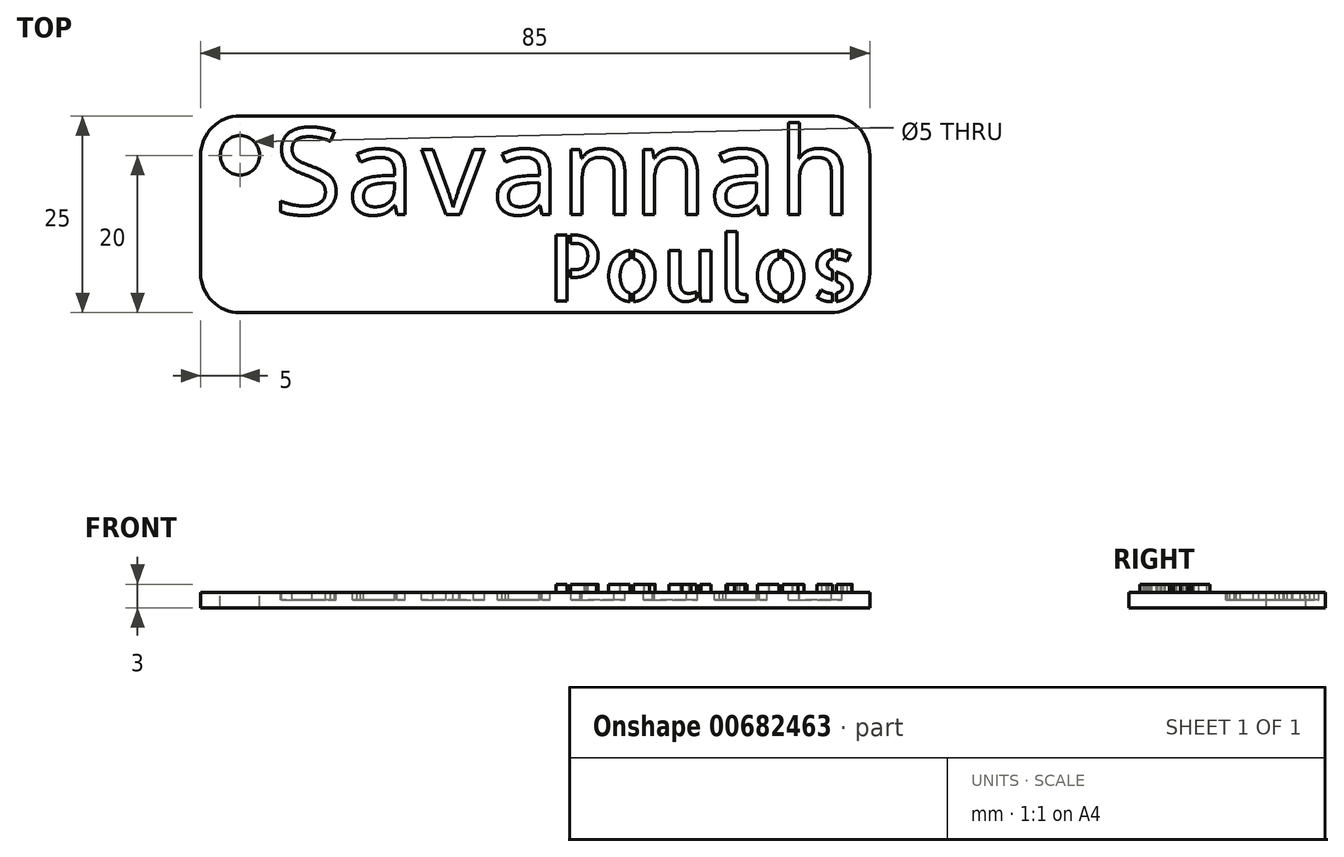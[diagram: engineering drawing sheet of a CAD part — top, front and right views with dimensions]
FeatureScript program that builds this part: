
annotation { "Feature Type Name" : "Feature", "Feature Type Description" : "" }
export const myFeature = defineFeature(function(context is Context, id is Id, definition is map)
    precondition{}
    {
        {
            var Q0;
            Q0=qCreatedBy(makeId("Top.planeOp"),FACE);
            var sketch = newSketch(context, id + "F0", { "sketchPlane" : qUnion([Q0])});
            skLineSegment(sketch, "E0.bottom", {"start": v(37.5, 12.5) * mm, "end": v(-37.5, 12.5) * mm});
            skLineSegment(sketch, "E0.top", {"start": v(37.5, -12.5) * mm, "end": v(-37.5, -12.5) * mm});
            skLineSegment(sketch, "E0.left", {"start": v(42.5, 7.5) * mm, "end": v(42.5, -7.5) * mm});
            skLineSegment(sketch, "E0.right", {"start": v(-42.5, 7.5) * mm, "end": v(-42.5, -7.5) * mm});
            skPoint(sketch, "E0.middle", {"position": v(0, 0) * mm});
            skPoint(sketch, "E1.visualSharp", {"position": v(-42.5, 12.5) * mm});
            skArc(sketch, "E1.filletArc", {"start": v(-37.5, 12.5) * mm, "mid": v(-41.04, 11.04) * mm, "end": v(-42.5, 7.5) * mm});
            skPoint(sketch, "E2.visualSharp", {"position": v(-42.5, -12.5) * mm});
            skArc(sketch, "E2.filletArc", {"start": v(-42.5, -7.5) * mm, "mid": v(-41.04, -11.04) * mm, "end": v(-37.5, -12.5) * mm});
            skPoint(sketch, "E3.visualSharp", {"position": v(42.5, -12.5) * mm});
            skArc(sketch, "E3.filletArc", {"start": v(37.5, -12.5) * mm, "mid": v(41.04, -11.04) * mm, "end": v(42.5, -7.5) * mm});
            skPoint(sketch, "E4.visualSharp", {"position": v(42.5, 12.5) * mm});
            skArc(sketch, "E4.filletArc", {"start": v(42.5, 7.5) * mm, "mid": v(41.04, 11.04) * mm, "end": v(37.5, 12.5) * mm});
            skSolve(sketch);
        }
        {
            var Q0;
            Q0 = qSketchRegion(id + "F0", true);
            extrude(context, id + "F1", {"entities" : qUnion([Q0]), "depth" : 2 * mm, "offsetDistance" : 25 * mm});
        }
        {
            var Q0;
            Q0=makeQuery(id+"F1.opExtrude","CAP_FACE",FACE,{"disambiguationData":[OSD([sQuery(id+"F0.wireOp",EDGE,"E0.bottom"),sQuery(id+"F0.wireOp",EDGE,"E0.top"),sQuery(id+"F0.wireOp",EDGE,"E0.left"),sQuery(id+"F0.wireOp",EDGE,"E0.right"),sQuery(id+"F0.wireOp",EDGE,"E1.filletArc"),sQuery(id+"F0.wireOp",EDGE,"E2.filletArc"),sQuery(id+"F0.wireOp",EDGE,"E3.filletArc"),sQuery(id+"F0.wireOp",EDGE,"E4.filletArc")])],"isStart":false});
            var sketch = newSketch(context, id + "F2", { "sketchPlane" : qUnion([Q0])});
            skPoint(sketch, "E5", {"position": v(-37.5, 7.5) * mm});
            skSolve(sketch);
        }
        {
            var Q0;
            Q0=sQuery(id+"F2.wireOp",VERTEX,"E5");
            var Q1;
            Q1=makeQuery(id+"F1.opExtrude","SWEPT_BODY",BODY,{"disambiguationData":[OSD([sQuery(id+"F0.wireOp",EDGE,"E0.bottom"),sQuery(id+"F0.wireOp",EDGE,"E0.top"),sQuery(id+"F0.wireOp",EDGE,"E0.left"),sQuery(id+"F0.wireOp",EDGE,"E0.right"),sQuery(id+"F0.wireOp",EDGE,"E1.filletArc"),sQuery(id+"F0.wireOp",EDGE,"E2.filletArc"),sQuery(id+"F0.wireOp",EDGE,"E3.filletArc"),sQuery(id+"F0.wireOp",EDGE,"E4.filletArc")])]});
            hole(context, id + "F3", {"style" : HoleStyle.SIMPLE, "endStyle" : HoleEndStyle.THROUGH, "holeDiameter" : 5 * mm, "majorDiameter" : 5 * mm, "isTappedThrough" : true, "tappedDepth" : 12 * mm, "tapClearance" : 3, "locations" : qUnion([Q0]), "scope" : qUnion([Q1])});
        }
        {
            var Q0;
            Q0=makeQuery(id+"F1.opExtrude","CAP_FACE",FACE,{"disambiguationData":[OSD([sQuery(id+"F0.wireOp",EDGE,"E0.bottom"),sQuery(id+"F0.wireOp",EDGE,"E0.top"),sQuery(id+"F0.wireOp",EDGE,"E0.left"),sQuery(id+"F0.wireOp",EDGE,"E0.right"),sQuery(id+"F0.wireOp",EDGE,"E1.filletArc"),sQuery(id+"F0.wireOp",EDGE,"E2.filletArc"),sQuery(id+"F0.wireOp",EDGE,"E3.filletArc"),sQuery(id+"F0.wireOp",EDGE,"E4.filletArc")])],"isStart":false});
            var sketch = newSketch(context, id + "F4", { "sketchPlane" : qUnion([Q0])});
            skText(sketch, "E6", { "text": "Savannah", "fontName": "DroidSansMono.ttf"});
            const initialGuessF4  = {"E6": [-0.03343, 0, 1, 0, 0.01104]};
            skSetInitialGuess(sketch, initialGuessF4);
            skSolve(sketch);
        }
        {
            var Q0;
            Q0 = qSketchRegion(id + "F4", true);
            extrude(context, id + "F5", {"entities" : qUnion([Q0]), "operationType" : NewBodyOperationType.REMOVE, "oppositeDirection" : true, "depth" : 1 * mm, "offsetDistance" : 25 * mm});
        }
        {
            var Q0;
            {var subQ0=sQuery(id+"F0.wireOp",EDGE,"E0.bottom");var subQ1=sQuery(id+"F0.wireOp",EDGE,"E0.left");var subQ2=sQuery(id+"F0.wireOp",EDGE,"E0.right");var subQ3=sQuery(id+"F0.wireOp",EDGE,"E1.filletArc");var subQ4=sQuery(id+"F0.wireOp",EDGE,"E2.filletArc");var subQ5=sQuery(id+"F0.wireOp",EDGE,"E4.filletArc");var subQ6=sQuery(id+"F0.wireOp",EDGE,"E3.filletArc");var subQ7=sQuery(id+"F0.wireOp",EDGE,"E0.top");Q0=makeQuery(id+"F5.boolean.opBoolean","SPLIT",FACE,{"disambiguationData":[TD([makeQuery(id+"F1.opExtrude","SWEPT_FACE",FACE,{"disambiguationData":[OSD([subQ0])]})])],"derivedFrom":makeQuery(id+"F1.opExtrude","CAP_FACE",FACE,{"disambiguationData":[OSD([subQ0,subQ7,subQ1,subQ2,subQ3,subQ4,subQ6,subQ5])],"isStart":false})});}
            var sketch = newSketch(context, id + "F6", { "sketchPlane" : qUnion([Q0])});
            skText(sketch, "E7", { "text": "Poulos", "fontName": "AllertaStencil-Regular.ttf"});
            const initialGuessF6  = {"E7": [0.00162, -0.01104, 1, 0, 0.0084]};
            skSetInitialGuess(sketch, initialGuessF6);
            skSolve(sketch);
        }
        {
            var Q0;
            Q0 = qSketchRegion(id + "F6", true);
            extrude(context, id + "F7", {"entities" : qUnion([Q0]), "operationType" : NewBodyOperationType.ADD, "depth" : 1 * mm, "offsetDistance" : 25 * mm});
        }
    });
